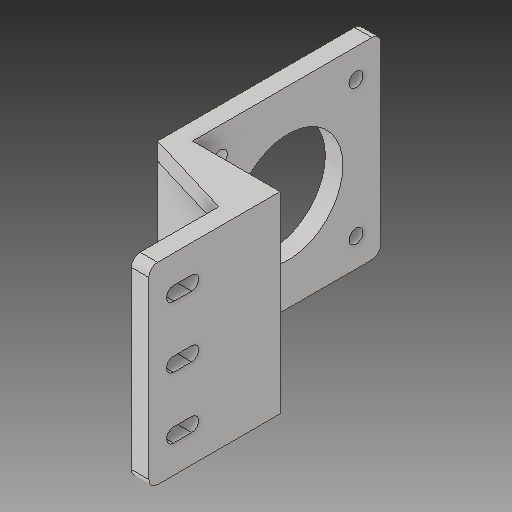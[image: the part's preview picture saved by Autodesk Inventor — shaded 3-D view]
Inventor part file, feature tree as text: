
AUTODESK INVENTOR PART (.ipt)
format: ipt  version: 2018 (Build 220112000, 112)  size: 176,640 bytes
history: native  units: in
note: dims shown in document units (in); Inventor stores cm internally (conversion verified against a paired STEP export)
features: extrude x4, sketch x4, fillet x1, projected_geometry x1
ambient origin geometry x8: Origin, YZ Plane, XZ Plane, XY Plane, X Axis, Y Axis, Z Axis, Center Point
bodies: Solid1 (feature_tree)
feature tree (10):
  extrude  "Extrusion1"  Depth=1.6929in
  extrude  "Extrusion2"  Depth=0.1575in
  extrude  "Extrusion3"  Depth=0.7874in
  extrude  "Extrusion4"  Depth=1.7323in TaperAngle=0.0deg
  fillet  "Fillet1"  Radius=0.126in
  sketch  "Sketch1"  dims[d0=0.7874in d1=1.6929in]
  sketch  "Sketch2"  dims[d2=0.1575in d3=0.1575in]
  projected_geometry  "Projected Loop1"
  sketch  "Sketch3"  dims[d4=1.1811in d5=0.7874in]
  sketch  "Sketch4"  dims[d6=0.1575in d7=1.7323in d8=0.0in d9=0.126in d10=0.9843in d11=0.8327in d12=1.2205in d13=1.2205in d14=0.6102in d15=0.6102in d16=1.7323in d17=0.0in d18=0.126in d19=0.1575in d20=0.315in d21=0.315in d22=1.7323in d23=0.0in d24=1.7323in d25=0.0in d26=0.1575in d27=0.1575in d28=0.0787in]
